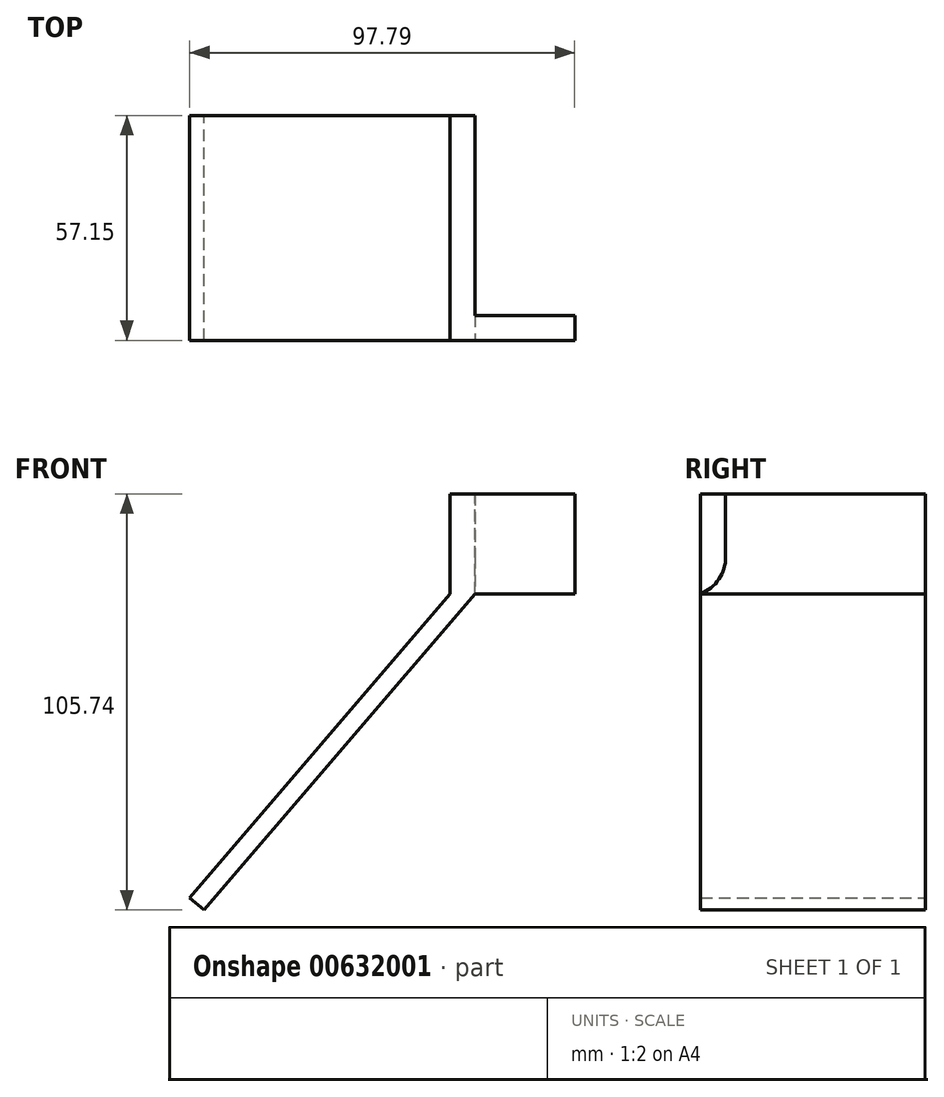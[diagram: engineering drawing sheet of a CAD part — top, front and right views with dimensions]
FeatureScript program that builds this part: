
annotation { "Feature Type Name" : "Feature", "Feature Type Description" : "" }
export const myFeature = defineFeature(function(context is Context, id is Id, definition is map)
    precondition{}
    {
        {
            var Q0;
            Q0=qCreatedBy(makeId("Front.planeOp"),FACE);
            var sketch = newSketch(context, id + "F0", { "sketchPlane" : qUnion([Q0])});
            skLineSegment(sketch, "E0", {"start": v(30.3, 56.06) * mm, "end": v(30.3, 30.66) * mm});
            skLineSegment(sketch, "E1", {"start": v(30.3, 30.66) * mm, "end": v(-35.75, -46.55) * mm});
            skLineSegment(sketch, "E2", {"start": v(-35.75, -46.55) * mm, "end": v(-32.08, -49.68) * mm});
            skLineSegment(sketch, "E3", {"start": v(-32.08, -49.68) * mm, "end": v(36.64, 30.66) * mm});
            skLineSegment(sketch, "E4", {"start": v(36.64, 30.66) * mm, "end": v(36.64, 56.06) * mm});
            skLineSegment(sketch, "E5", {"start": v(36.64, 56.06) * mm, "end": v(30.3, 56.06) * mm});
            skSolve(sketch);
        }
        {
            var Q0;
            Q0=makeQuery(id+"F0.imprint","IMPRINT",FACE,{"disambiguationData":[TD([[makeQuery(id+"F0.imprint","IMPRINT",EDGE,{"derivedFrom":sQuery(id+"F0.wireOp",EDGE,"E0")}),1.0]])]});
            var Q1;
            Q1=sQuery(id+"F0.wireOp",EDGE,"E0");
            var Q2;
            Q2=sQuery(id+"F0.wireOp",EDGE,"E1");
            var Q3;
            Q3=sQuery(id+"F0.wireOp",EDGE,"E2");
            var Q4;
            Q4=sQuery(id+"F0.wireOp",EDGE,"E3");
            var Q5;
            Q5=sQuery(id+"F0.wireOp",EDGE,"E4");
            var Q6;
            Q6=sQuery(id+"F0.wireOp",EDGE,"E5");
            extrude(context, id + "F1", {"entities" : qUnion([Q0]), "surfaceEntities" : qUnion([Q1, Q2, Q3, Q4, Q5, Q6]), "depth" : 57.15 * mm, "offsetDistance" : 25.4 * mm});
        }
        {
            var Q0;
            Q0=makeQuery(id+"F1.opExtrude","SWEPT_FACE",FACE,{"disambiguationData":[OSD([sQuery(id+"F0.wireOp",EDGE,"E4")])]});
            var sketch = newSketch(context, id + "F2", { "sketchPlane" : qUnion([Q0])});
            skLineSegment(sketch, "E6.bottom", {"start": v(-57.15, 56.06) * mm, "end": v(-50.8, 56.06) * mm});
            skLineSegment(sketch, "E6.top", {"start": v(-57.15, 30.66) * mm, "end": v(-50.8, 30.66) * mm});
            skLineSegment(sketch, "E6.left", {"start": v(-57.15, 56.06) * mm, "end": v(-57.15, 30.66) * mm});
            skLineSegment(sketch, "E6.right", {"start": v(-50.8, 56.06) * mm, "end": v(-50.8, 30.66) * mm});
            skSolve(sketch);
        }
        {
            var Q0;
            Q0=makeQuery(id+"F2.imprint","IMPRINT",FACE,{"disambiguationData":[TD([[makeQuery(id+"F2.imprint","IMPRINT",EDGE,{"derivedFrom":sQuery(id+"F2.wireOp",EDGE,"E6.bottom")}),-1.0]])]});
            extrude(context, id + "F3", {"entities" : qUnion([Q0]), "operationType" : NewBodyOperationType.ADD, "depth" : 25.4 * mm, "offsetDistance" : 25.4 * mm});
        }
        {
            var Q0;
            Q0=makeQuery(id+"F3.opExtrude","SWEPT_EDGE",EDGE,{"disambiguationData":[OSD([sQuery(id+"F0.wireOp",EDGE,"E3"),sQuery(id+"F0.wireOp",EDGE,"E4"),sQuery(id+"F2.wireOp",EDGE,"E6.top"),sQuery(id+"F2.wireOp",EDGE,"E6.right")])]});
            fillet(context, id + "F4", {"entities" : qUnion([Q0]), "radius" : 10.16 * mm, "tangentPropagation" : true, "allowEdgeOverflow" : false});
        }
    });
